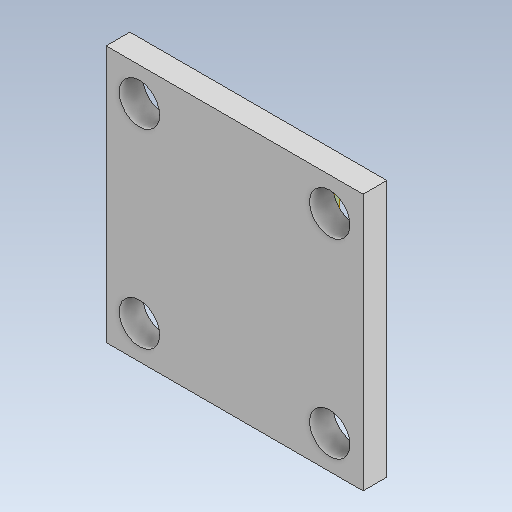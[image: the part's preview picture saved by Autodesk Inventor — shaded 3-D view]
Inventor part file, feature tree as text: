
AUTODESK INVENTOR PART (.ipt)
format: ipt  version: 2025.2 (Build 292293000, 293)  size: 328,192 bytes
history: native  units: mm
features: sketch x3, plane x2, extrude x2, hole x1
ambient origin geometry x8: Origin, YZ Plane, XZ Plane, XY Plane, X Axis, Y Axis, Z Axis, Center Point
bodies: Volumenkörper1 (feature_tree)
feature tree (8):
  sketch  "Skizze1"  dims[d0=16.0mm d1=12.0mm]
  plane  "Arbeitsebene1"
  extrude  "Extrusion2"  Depth=12.0mm
  plane  "Arbeitsebene2"
  hole  "Bohrung1"  [1 undecoded]
  extrude  "Extrusion4"  Depth=4.0mm
  sketch  "Skizze2"  dims[d2=5.0mm d3=5.0mm]
  sketch  "Skizze4"  dims[d9=5.0mm d10=0.0mm d11=16.0mm d12=14.0mm d13=16.0mm d14=14.0mm d35=54.0mm d36=54.0mm d37=8.5mm d38=6.0mm d39=4.0mm d40=2.0mm d41=90.0deg d42=5.0mm d43=0.0mm d44=7.0mm d45=7.0mm d46=7.0mm d47=7.0mm d48=7.0mm d49=7.0mm d50=7.0mm d51=7.0mm d52=40.0mm d53=40.0mm d54=40.0mm d55=40.0mm d56=1.0mm d57=1.0mm d58=1.0mm d60=1.75mm d61=1.75mm d63=8.5mm d64=1.0mm d65=1.0mm d67=1.0mm d69=12.5mm d70=1.0mm d71=1.75mm d72=1.75mm d74=7.0mm d76=7.0mm d77=5.0mm d78=5.0mm d80=1.0mm d81=1.0mm d82=1.0mm d83=1.0mm d84=4.0mm d85=0.0mm]
note: 1 required parameter value undecoded (feature->parameter linkage not recoverable at this tier; creation-order binding heuristic only, values carry confidence <= 0.55)
